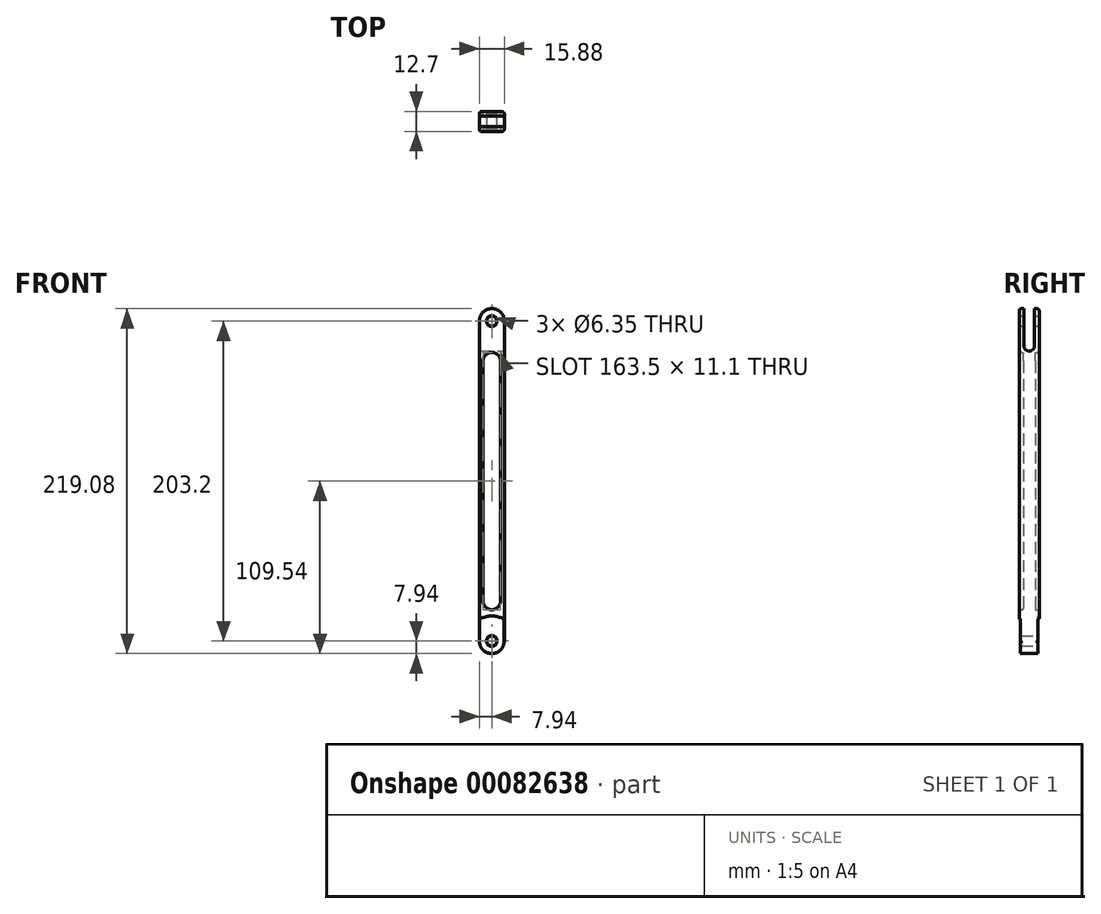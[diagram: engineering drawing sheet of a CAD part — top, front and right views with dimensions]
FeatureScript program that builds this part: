
annotation { "Feature Type Name" : "Feature", "Feature Type Description" : "" }
export const myFeature = defineFeature(function(context is Context, id is Id, definition is map)
    precondition{}
    {
        {
            var Q0;
            Q0=qCreatedBy(makeId("Front.planeOp"),FACE);
            var sketch = newSketch(context, id + "F0", { "sketchPlane" : qUnion([Q0])});
            skArc(sketch, "E0", {"start": v(7.94, 0) * mm, "mid": v(0, 7.94) * mm, "end": v(-7.94, 0) * mm});
            skArc(sketch, "E1", {"start": v(-7.94, -203.2) * mm, "mid": v(0, -211.14) * mm, "end": v(7.94, -203.2) * mm});
            skCircle(sketch, "E2", {"center": v(0, 0) * mm, "radius": 3.18 * mm});
            skCircle(sketch, "E3", {"center": v(0, -203.2) * mm, "radius": 3.17 * mm});
            skLineSegment(sketch, "E4", {"start": v(-7.94, 0) * mm, "end": v(-7.94, -203.2) * mm});
            skLineSegment(sketch, "E5", {"start": v(-7.94, -203.2) * mm, "end": v(7.94, -203.2) * mm});
            skLineSegment(sketch, "E6", {"start": v(7.94, -203.2) * mm, "end": v(7.94, 0) * mm});
            skSolve(sketch);
        }
        {
            var Q0;
            Q0 = qSketchRegion(id + "F0", true);
            extrude(context, id + "F1", {"entities" : qUnion([Q0]), "endBound" : BoundingType.SYMMETRIC, "depth" : 12.7 * mm});
        }
        {
            var Q0;
            Q0=makeQuery(id+"F1.opExtrude","CAP_FACE",FACE,{"disambiguationData":[OSD([sQuery(id+"F0.wireOp",EDGE,"E0"),sQuery(id+"F0.wireOp",EDGE,"E1"),sQuery(id+"F0.wireOp",EDGE,"E2"),sQuery(id+"F0.wireOp",EDGE,"E3"),sQuery(id+"F0.wireOp",EDGE,"E4"),sQuery(id+"F0.wireOp",EDGE,"E6")])],"isStart":false});
            var sketch = newSketch(context, id + "F2", { "sketchPlane" : qUnion([Q0])});
            skCircle(sketch, "E7", {"center": v(0, -203.2) * mm, "radius": 15.88 * mm});
            skSolve(sketch);
        }
        {
            var Q0;
            Q0 = qSketchRegion(id + "F2", true);
            extrude(context, id + "F3", {"entities" : qUnion([Q0]), "operationType" : NewBodyOperationType.REMOVE, "oppositeDirection" : true, "depth" : 0.81 * mm});
        }
        {
            var Q0;
            Q0=makeQuery(id+"F1.opExtrude","CAP_FACE",FACE,{"disambiguationData":[OSD([sQuery(id+"F0.wireOp",EDGE,"E0"),sQuery(id+"F0.wireOp",EDGE,"E1"),sQuery(id+"F0.wireOp",EDGE,"E2"),sQuery(id+"F0.wireOp",EDGE,"E3"),sQuery(id+"F0.wireOp",EDGE,"E4"),sQuery(id+"F0.wireOp",EDGE,"E6")])],"isStart":true});
            var sketch = newSketch(context, id + "F4", { "sketchPlane" : qUnion([Q0])});
            skCircle(sketch, "E8", {"center": v(0, -203.2) * mm, "radius": 15.88 * mm});
            skSolve(sketch);
        }
        {
            var Q0;
            Q0 = qSketchRegion(id + "F4", true);
            extrude(context, id + "F5", {"entities" : qUnion([Q0]), "operationType" : NewBodyOperationType.REMOVE, "oppositeDirection" : true, "depth" : 0.81 * mm});
        }
        {
            var Q0;
            Q0=makeQuery(id+"F1.opExtrude","CAP_FACE",FACE,{"disambiguationData":[OSD([sQuery(id+"F0.wireOp",EDGE,"E0"),sQuery(id+"F0.wireOp",EDGE,"E1"),sQuery(id+"F0.wireOp",EDGE,"E2"),sQuery(id+"F0.wireOp",EDGE,"E3"),sQuery(id+"F0.wireOp",EDGE,"E4"),sQuery(id+"F0.wireOp",EDGE,"E6")])],"isStart":false});
            var sketch = newSketch(context, id + "F6", { "sketchPlane" : qUnion([Q0])});
            skArc(sketch, "E9", {"start": v(5.55, -25.4) * mm, "mid": v(0, -19.85) * mm, "end": v(-5.55, -25.4) * mm});
            skArc(sketch, "E10", {"start": v(-5.55, -177.8) * mm, "mid": v(0, -183.35) * mm, "end": v(5.55, -177.8) * mm});
            skLineSegment(sketch, "E11", {"start": v(-5.55, -177.8) * mm, "end": v(-5.55, -25.4) * mm});
            skLineSegment(sketch, "E12", {"start": v(5.55, -25.4) * mm, "end": v(5.55, -177.8) * mm});
            skPoint(sketch, "E13", {"position": v(0, -203.2) * mm});
            skPoint(sketch, "E14", {"position": v(27.4, -180.95) * mm});
            skSolve(sketch);
        }
        {
            var Q0;
            Q0 = qSketchRegion(id + "F6", true);
            extrude(context, id + "F7", {"entities" : qUnion([Q0]), "operationType" : NewBodyOperationType.REMOVE, "oppositeDirection" : true, "depth" : 2.54 * mm});
        }
        {
            var Q0;
            Q0=makeQuery(id+"F1.opExtrude","CAP_FACE",FACE,{"disambiguationData":[OSD([sQuery(id+"F0.wireOp",EDGE,"E0"),sQuery(id+"F0.wireOp",EDGE,"E1"),sQuery(id+"F0.wireOp",EDGE,"E2"),sQuery(id+"F0.wireOp",EDGE,"E3"),sQuery(id+"F0.wireOp",EDGE,"E4"),sQuery(id+"F0.wireOp",EDGE,"E6")])],"isStart":true});
            var sketch = newSketch(context, id + "F8", { "sketchPlane" : qUnion([Q0])});
            skPoint(sketch, "E15", {"position": v(0, -177.8) * mm});
            skPoint(sketch, "E16", {"position": v(0, -203.2) * mm});
            skCircle(sketch, "E17", {"center": v(0, -177.8) * mm, "radius": 5.55 * mm});
            skPoint(sketch, "E18", {"position": v(0, -25.4) * mm});
            skCircle(sketch, "E19", {"center": v(0, -25.4) * mm, "radius": 5.55 * mm});
            skLineSegment(sketch, "E20", {"start": v(-5.55, -25.4) * mm, "end": v(-5.55, -177.8) * mm});
            skLineSegment(sketch, "E21", {"start": v(5.55, -25.4) * mm, "end": v(5.55, -177.8) * mm});
            skSolve(sketch);
        }
        {
            var Q0;
            Q0 = qSketchRegion(id + "F8", true);
            extrude(context, id + "F9", {"entities" : qUnion([Q0]), "operationType" : NewBodyOperationType.REMOVE, "oppositeDirection" : true, "depth" : 2.54 * mm});
        }
        {
            var Q0;
            Q0=qCreatedBy(makeId("Right.planeOp"),FACE);
            var sketch = newSketch(context, id + "F10", { "sketchPlane" : qUnion([Q0])});
            skLineSegment(sketch, "E22.bottom", {"start": v(-3.3, 10.07) * mm, "end": v(3.3, 10.07) * mm});
            skLineSegment(sketch, "E22.top", {"start": v(-3.3, -19.05) * mm, "end": v(3.3, -19.05) * mm});
            skLineSegment(sketch, "E22.left", {"start": v(-3.3, 10.07) * mm, "end": v(-3.3, -19.05) * mm});
            skLineSegment(sketch, "E22.right", {"start": v(3.3, 10.07) * mm, "end": v(3.3, -19.05) * mm});
            skSolve(sketch);
        }
        {
            var Q0;
            Q0 = qSketchRegion(id + "F10", true);
            extrude(context, id + "F11", {"entities" : qUnion([Q0]), "operationType" : NewBodyOperationType.REMOVE, "endBound" : BoundingType.SYMMETRIC, "depth" : 25.4 * mm});
        }
        {
            var Q0;
            Q0=makeQuery(id+"F11.boolean.opBoolean","COPY",EDGE,{"derivedFrom":makeQuery(id+"F11.opExtrude","SWEPT_EDGE",EDGE,{"disambiguationData":[OSD([sQuery(id+"F10.wireOp",EDGE,"E22.top"),sQuery(id+"F10.wireOp",EDGE,"E22.left")])]})});
            var Q1;
            Q1=makeQuery(id+"F11.boolean.opBoolean","COPY",EDGE,{"derivedFrom":makeQuery(id+"F11.opExtrude","SWEPT_EDGE",EDGE,{"disambiguationData":[OSD([sQuery(id+"F10.wireOp",EDGE,"E22.top"),sQuery(id+"F10.wireOp",EDGE,"E22.right")])]})});
            fillet(context, id + "F12", {"entities" : qUnion([Q0, Q1]), "radius" : 3.3 * mm, "tangentPropagation" : true, "allowEdgeOverflow" : false});
        }
        {
            var Q0;
            Q0=makeQuery(id+"F1.opExtrude","CAP_EDGE",EDGE,{"disambiguationData":[OSD([sQuery(id+"F0.wireOp",EDGE,"E6")])],"isStart":false});
            var Q1;
            Q1=makeQuery(id+"F1.opExtrude","CAP_EDGE",EDGE,{"disambiguationData":[OSD([sQuery(id+"F0.wireOp",EDGE,"E6")])],"isStart":true});
            fillet(context, id + "F13", {"entities" : qUnion([Q0, Q1]), "radius" : 1.52 * mm, "tangentPropagation" : true, "allowEdgeOverflow" : false});
        }
        {
            var Q0;
            Q0=makeQuery(id+"F7.boolean.opBoolean","COPY",EDGE,{"derivedFrom":makeQuery(id+"F7.opExtrude","CAP_EDGE",EDGE,{"disambiguationData":[OSD([sQuery(id+"F6.wireOp",EDGE,"E9")])],"isStart":false})});
            var Q1;
            Q1=makeQuery(id+"F9.boolean.opBoolean","COPY",EDGE,{"derivedFrom":makeQuery(id+"F9.opExtrude","CAP_EDGE",EDGE,{"disambiguationData":[OSD([sQuery(id+"F8.wireOp",EDGE,"E19")])],"isStart":true})});
            fillet(context, id + "F14", {"entities" : qUnion([Q0, Q1]), "radius" : 0.76 * mm, "tangentPropagation" : true, "allowEdgeOverflow" : false});
        }
        {
            var Q0;
            Q0=makeQuery(id+"F1.opExtrude","CAP_EDGE",EDGE,{"disambiguationData":[OSD([sQuery(id+"F0.wireOp",EDGE,"E2")])],"isStart":true});
            var Q1;
            Q1=makeQuery(id+"F1.opExtrude","CAP_EDGE",EDGE,{"disambiguationData":[OSD([sQuery(id+"F0.wireOp",EDGE,"E2")])],"isStart":false});
            var Q2;
            Q2=makeQuery(id+"F3.boolean.opBoolean","INTERSECT",EDGE,{"derivedFrom":[makeQuery(id+"F1.opExtrude","SWEPT_FACE",FACE,{"disambiguationData":[OSD([sQuery(id+"F0.wireOp",EDGE,"E3")])]}),makeQuery(id+"F3.opExtrude","CAP_FACE",FACE,{"disambiguationData":[OSD([sQuery(id+"F2.wireOp",EDGE,"E7")])],"isStart":false})]});
            var Q3;
            Q3=makeQuery(id+"F5.boolean.opBoolean","INTERSECT",EDGE,{"derivedFrom":[makeQuery(id+"F1.opExtrude","SWEPT_FACE",FACE,{"disambiguationData":[OSD([sQuery(id+"F0.wireOp",EDGE,"E3")])]}),makeQuery(id+"F5.opExtrude","CAP_FACE",FACE,{"disambiguationData":[OSD([sQuery(id+"F4.wireOp",EDGE,"E8")])],"isStart":false})]});
            chamfer(context, id + "F15", {"entities" : qUnion([Q0, Q1, Q2, Q3]), "width" : 0.25 * mm, "tangentPropagation" : true});
        }
    });
